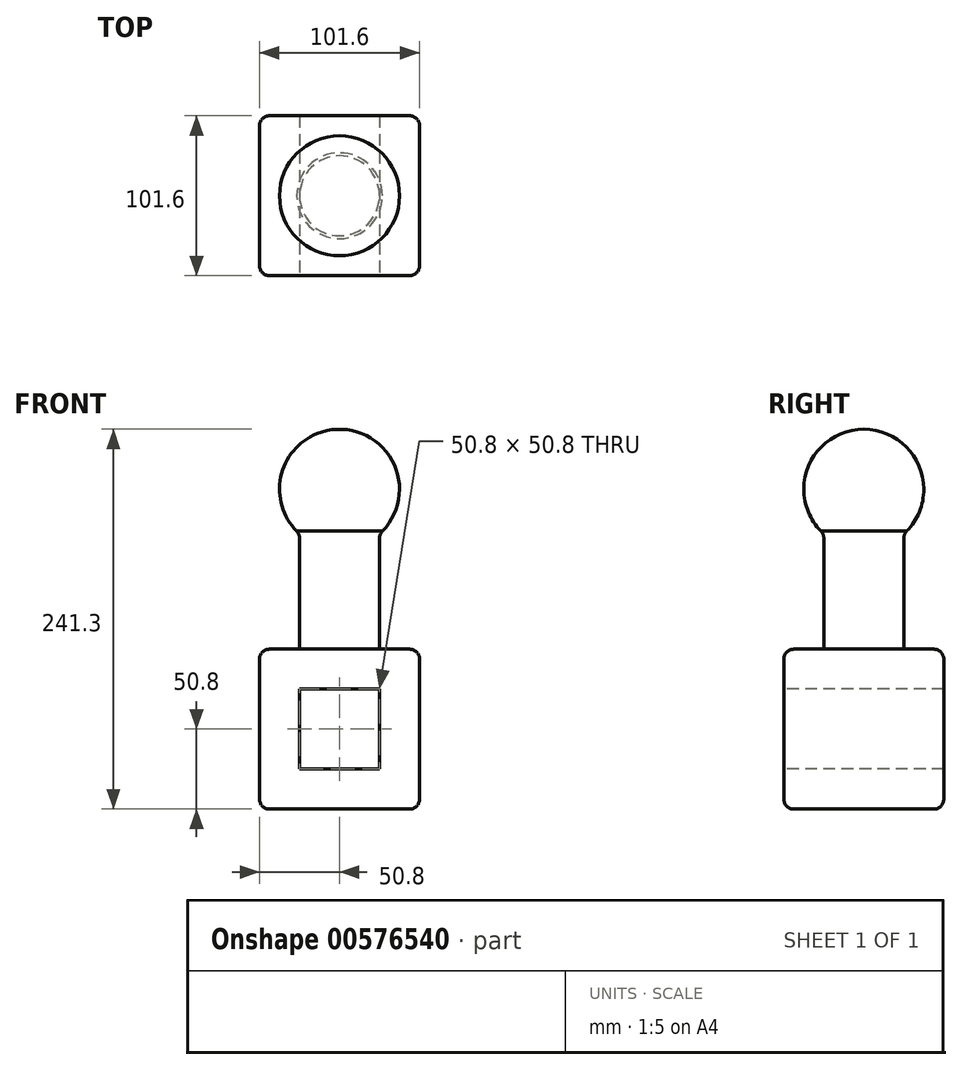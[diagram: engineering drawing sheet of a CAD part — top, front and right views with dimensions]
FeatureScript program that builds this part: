
annotation { "Feature Type Name" : "Feature", "Feature Type Description" : "" }
export const myFeature = defineFeature(function(context is Context, id is Id, definition is map)
    precondition{}
    {
        {
            var Q0;
            Q0=qCreatedBy(makeId("Top.planeOp"),FACE);
            var sketch = newSketch(context, id + "F0", { "sketchPlane" : qUnion([Q0])});
            skLineSegment(sketch, "E0.bottom", {"start": v(50.8, -50.8) * mm, "end": v(-50.8, -50.8) * mm});
            skLineSegment(sketch, "E0.top", {"start": v(50.8, 50.8) * mm, "end": v(-50.8, 50.8) * mm});
            skLineSegment(sketch, "E0.left", {"start": v(50.8, -50.8) * mm, "end": v(50.8, 50.8) * mm});
            skLineSegment(sketch, "E0.right", {"start": v(-50.8, -50.8) * mm, "end": v(-50.8, 50.8) * mm});
            skPoint(sketch, "E0.middle", {"position": v(0, 0) * mm});
            skSolve(sketch);
        }
        {
            var Q0;
            Q0 = qSketchRegion(id + "F0", true);
            extrude(context, id + "F1", {"entities" : qUnion([Q0]), "depth" : 101.6 * mm, "offsetDistance" : 25.4 * mm});
        }
        {
            var Q0;
            Q0=makeQuery(id+"F1.opExtrude","CAP_FACE",FACE,{"disambiguationData":[OSD([sQuery(id+"F0.wireOp",EDGE,"E0.bottom"),sQuery(id+"F0.wireOp",EDGE,"E0.top"),sQuery(id+"F0.wireOp",EDGE,"E0.left"),sQuery(id+"F0.wireOp",EDGE,"E0.right")])],"isStart":false});
            var sketch = newSketch(context, id + "F2", { "sketchPlane" : qUnion([Q0])});
            skCircle(sketch, "E1", {"center": v(0, 0) * mm, "radius": 25.4 * mm});
            skSolve(sketch);
        }
        {
            var Q0;
            Q0 = qSketchRegion(id + "F2", true);
            extrude(context, id + "F3", {"entities" : qUnion([Q0]), "operationType" : NewBodyOperationType.ADD, "depth" : 101.6 * mm, "offsetDistance" : 25.4 * mm});
        }
        {
            var Q0;
            Q0=makeQuery(id+"F3.opExtrude","CAP_FACE",FACE,{"disambiguationData":[OSD([sQuery(id+"F2.wireOp",EDGE,"E1")])],"isStart":false});
            var sketch = newSketch(context, id + "F4", { "sketchPlane" : qUnion([Q0])});
            skArc(sketch, "E2", {"start": v(0, -38.1) * mm, "mid": v(38.1, 0) * mm, "end": v(0, 38.1) * mm});
            skLineSegment(sketch, "E3", {"start": v(0, 38.1) * mm, "end": v(0, -38.1) * mm});
            skSolve(sketch);
        }
        {
            var Q0;
            {var subQ0=sQuery(id+"F4.wireOp",EDGE,"E2");Q0=makeQuery(id+"F4.imprint","IMPRINT",FACE,{"disambiguationData":[TD([[makeQuery(id+"F4.imprint","IMPRINT",EDGE,{"derivedFrom":subQ0}),1.0]])]});}
            var Q1;
            {var subQ0=sQuery(id+"F4.wireOp",EDGE,"E3");var subQ1=makeQuery(id+"F3.opExtrude","CAP_EDGE",EDGE,{"disambiguationData":[OSD([sQuery(id+"F2.wireOp",EDGE,"E1")])],"isStart":false});var subQ2=makeQuery(id+"F4.imprint","INTERSECT",VERTEX,{"disambiguationData":[OD(0.0)],"derivedFrom":[subQ1,subQ0]});Q1=makeQuery(id+"F4.imprint","IMPRINT",FACE,{"disambiguationData":[TD([[makeQuery(id+"F4.imprint","IMPRINT",EDGE,{"disambiguationData":[TD([[subQ2,-1.0]])],"derivedFrom":subQ0}),1.0]])]});}
            var Q2;
            Q2=sQuery(id+"F4.wireOp",EDGE,"E3");
            revolve(context, id + "F5", {"operationType" : NewBodyOperationType.ADD, "entities" : qUnion([Q0, Q1]), "axis" : qUnion([Q2]), "revolveType" : RevolveType.FULL});
        }
        {
            var Q0;
            Q0=makeQuery(id+"F1.opExtrude","SWEPT_FACE",FACE,{"disambiguationData":[OSD([sQuery(id+"F0.wireOp",EDGE,"E0.bottom")])]});
            var sketch = newSketch(context, id + "F6", { "sketchPlane" : qUnion([Q0])});
            skLineSegment(sketch, "E4.bottom", {"start": v(25.4, 25.4) * mm, "end": v(-25.4, 25.4) * mm});
            skLineSegment(sketch, "E4.top", {"start": v(25.4, 76.2) * mm, "end": v(-25.4, 76.2) * mm});
            skLineSegment(sketch, "E4.left", {"start": v(25.4, 25.4) * mm, "end": v(25.4, 76.2) * mm});
            skLineSegment(sketch, "E4.right", {"start": v(-25.4, 25.4) * mm, "end": v(-25.4, 76.2) * mm});
            skPoint(sketch, "E4.middle", {"position": v(0, 50.8) * mm});
            skPoint(sketch, "E4.middle.positionSnap0", {"position": v(50.8, 50.8) * mm});
            skPoint(sketch, "E4.centerSnap0", {"position": v(50.8, 50.8) * mm});
            skSolve(sketch);
        }
        {
            var Q0;
            Q0 = qSketchRegion(id + "F6", true);
            extrude(context, id + "F7", {"entities" : qUnion([Q0]), "operationType" : NewBodyOperationType.REMOVE, "oppositeDirection" : true, "depth" : 101.6 * mm, "offsetDistance" : 25.4 * mm});
        }
        {
            var Q0;
            Q0=makeQuery(id+"F1.opExtrude","CAP_EDGE",EDGE,{"disambiguationData":[OSD([sQuery(id+"F0.wireOp",EDGE,"E0.top")])],"isStart":false});
            var Q1;
            Q1=makeQuery(id+"F1.opExtrude","CAP_EDGE",EDGE,{"disambiguationData":[OSD([sQuery(id+"F0.wireOp",EDGE,"E0.left")])],"isStart":false});
            var Q2;
            Q2=makeQuery(id+"F1.opExtrude","CAP_EDGE",EDGE,{"disambiguationData":[OSD([sQuery(id+"F0.wireOp",EDGE,"E0.bottom")])],"isStart":false});
            var Q3;
            Q3=makeQuery(id+"F1.opExtrude","SWEPT_FACE",FACE,{"disambiguationData":[OSD([sQuery(id+"F0.wireOp",EDGE,"E0.right")])]});
            var Q4;
            Q4=makeQuery(id+"F1.opExtrude","SWEPT_EDGE",EDGE,{"disambiguationData":[OSD([sQuery(id+"F0.wireOp",EDGE,"E0.top"),sQuery(id+"F0.wireOp",EDGE,"E0.left")])]});
            var Q5;
            Q5=makeQuery(id+"F1.opExtrude","CAP_EDGE",EDGE,{"disambiguationData":[OSD([sQuery(id+"F0.wireOp",EDGE,"E0.top")])],"isStart":true});
            var Q6;
            Q6=makeQuery(id+"F1.opExtrude","SWEPT_EDGE",EDGE,{"disambiguationData":[OSD([sQuery(id+"F0.wireOp",EDGE,"E0.bottom"),sQuery(id+"F0.wireOp",EDGE,"E0.left")])]});
            var Q7;
            Q7=makeQuery(id+"F1.opExtrude","CAP_EDGE",EDGE,{"disambiguationData":[OSD([sQuery(id+"F0.wireOp",EDGE,"E0.bottom")])],"isStart":true});
            var Q8;
            Q8=makeQuery(id+"F1.opExtrude","CAP_EDGE",EDGE,{"disambiguationData":[OSD([sQuery(id+"F0.wireOp",EDGE,"E0.left")])],"isStart":true});
            var Q9;
            Q9=makeQuery(id+"F5.boolean.opBoolean","INTERSECT",EDGE,{"derivedFrom":[makeQuery(id+"F3.opExtrude","SWEPT_FACE",FACE,{"disambiguationData":[OSD([sQuery(id+"F2.wireOp",EDGE,"E1")])]}),makeQuery(id+"F5.opRevolve","SWEPT_FACE",FACE,{"disambiguationData":[OSD([sQuery(id+"F4.wireOp",EDGE,"E2")])]})]});
            fillet(context, id + "F8", {"entities" : qUnion([Q0, Q1, Q2, Q3, Q4, Q5, Q6, Q7, Q8, Q9]), "radius" : 6.35 * mm, "tangentPropagation" : true, "allowEdgeOverflow" : false});
        }
    });
